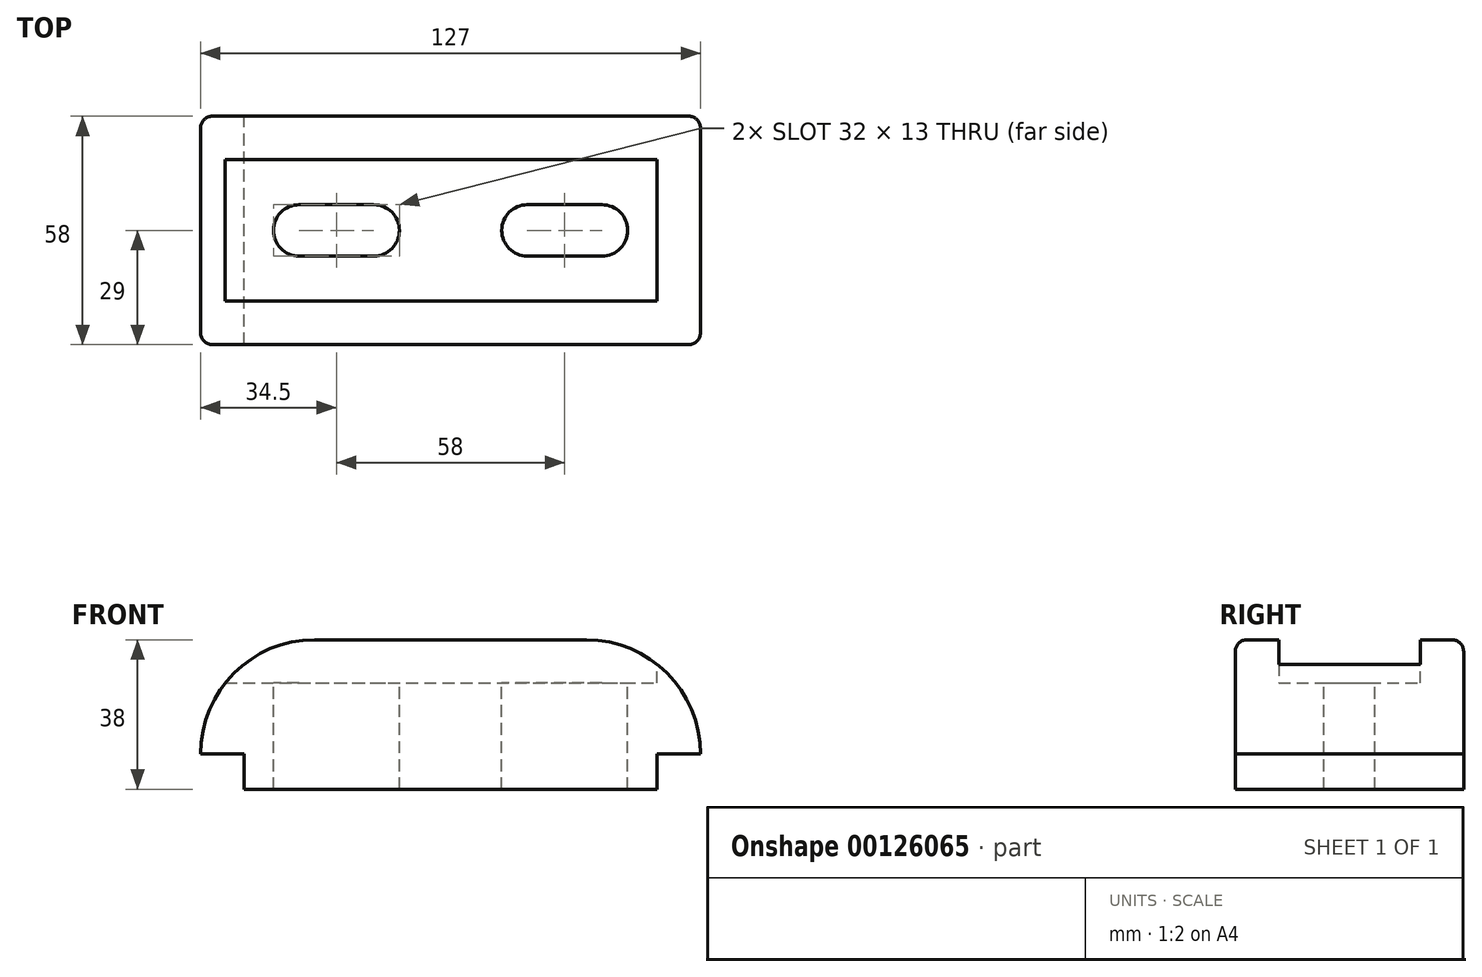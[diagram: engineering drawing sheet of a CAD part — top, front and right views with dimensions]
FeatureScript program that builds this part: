
annotation { "Feature Type Name" : "Feature", "Feature Type Description" : "" }
export const myFeature = defineFeature(function(context is Context, id is Id, definition is map)
    precondition{}
    {
        {
            var Q0;
            Q0=qCreatedBy(makeId("Front.planeOp"),FACE);
            var sketch = newSketch(context, id + "F0", { "sketchPlane" : qUnion([Q0])});
            skLineSegment(sketch, "E0", {"start": v(0, 0) * mm, "end": v(-52.5, 0) * mm});
            skLineSegment(sketch, "E1", {"start": v(-52.5, 0) * mm, "end": v(0, 0) * mm});
            skLineSegment(sketch, "E2.MirrorCS", {"start": v(52.5, 0) * mm, "end": v(0, 0) * mm});
            skLineSegment(sketch, "E3", {"start": v(-52.5, 0) * mm, "end": v(-52.5, 9) * mm});
            skLineSegment(sketch, "E4", {"start": v(-52.5, 9) * mm, "end": v(-63.5, 9) * mm});
            skLineSegment(sketch, "E5", {"start": v(-63.5, 9) * mm, "end": v(-63.5, 9) * mm});
            skLineSegment(sketch, "E6", {"start": v(-34.5, 38) * mm, "end": v(0, 38) * mm});
            skPoint(sketch, "E7.visualSharp", {"position": v(-63.5, 38) * mm});
            skArc(sketch, "E7.filletArc", {"start": v(-34.5, 38) * mm, "mid": v(-55, 29.5) * mm, "end": v(-63.5, 9) * mm});
            skLineSegment(sketch, "E8.MirrorCS", {"start": v(34.5, 38) * mm, "end": v(0, 38) * mm});
            skArc(sketch, "E9.MirrorCS", {"start": v(34.5, 38) * mm, "mid": v(55, 29.5) * mm, "end": v(63.5, 9) * mm});
            skLineSegment(sketch, "E10.MirrorCS", {"start": v(52.5, 9) * mm, "end": v(63.5, 9) * mm});
            skLineSegment(sketch, "E11.MirrorCS", {"start": v(52.5, 0) * mm, "end": v(52.5, 9) * mm});
            skSolve(sketch);
        }
        {
            var Q0;
            Q0 = qSketchRegion(id + "F0", true);
            extrude(context, id + "F1", {"entities" : qUnion([Q0]), "endBound" : BoundingType.SYMMETRIC, "depth" : 58 * mm});
        }
        {
            var Q0;
            Q0=makeQuery(id+"F1.opExtrude","SWEPT_FACE",FACE,{"disambiguationData":[OSD([sQuery(id+"F0.wireOp",EDGE,"E11.MirrorCS")])]});
            var sketch = newSketch(context, id + "F2", { "sketchPlane" : qUnion([Q0])});
            skLineSegment(sketch, "E12", {"start": v(18, 38) * mm, "end": v(-18, 38) * mm});
            skLineSegment(sketch, "E13", {"start": v(-18, 38) * mm, "end": v(-18, 27) * mm});
            skLineSegment(sketch, "E14", {"start": v(-18, 27) * mm, "end": v(18, 27) * mm});
            skLineSegment(sketch, "E15", {"start": v(18, 27) * mm, "end": v(18, 38) * mm});
            skSolve(sketch);
        }
        {
            var Q0;
            Q0 = qSketchRegion(id + "F2", true);
            extrude(context, id + "F3", {"entities" : qUnion([Q0]), "operationType" : NewBodyOperationType.REMOVE, "endBound" : BoundingType.THROUGH_ALL, "oppositeDirection" : true, "depth" : 25 * mm});
        }
        {
            var Q0;
            Q0=makeQuery(id+"F1.opExtrude","CAP_EDGE",EDGE,{"disambiguationData":[OSD([sQuery(id+"F0.wireOp",EDGE,"E6"),sQuery(id+"F0.wireOp",EDGE,"E8.MirrorCS")])],"isStart":true});
            var Q1;
            Q1=makeQuery(id+"F1.opExtrude","CAP_EDGE",EDGE,{"disambiguationData":[OSD([sQuery(id+"F0.wireOp",EDGE,"E6"),sQuery(id+"F0.wireOp",EDGE,"E8.MirrorCS")])],"isStart":false});
            fillet(context, id + "F4", {"entities" : qUnion([Q0, Q1]), "radius" : 3 * mm, "tangentPropagation" : true, "allowEdgeOverflow" : false});
        }
        {
            var Q0;
            Q0=makeQuery(id+"F3.boolean.opBoolean","COPY",FACE,{"derivedFrom":makeQuery(id+"F3.opExtrude","SWEPT_FACE",FACE,{"disambiguationData":[OSD([sQuery(id+"F2.wireOp",EDGE,"E14")])]})});
            var sketch = newSketch(context, id + "F5", { "sketchPlane" : qUnion([Q0])});
            skLineSegment(sketch, "E16.bottom", {"start": v(-38.5, -6.5) * mm, "end": v(-19.5, -6.5) * mm});
            skLineSegment(sketch, "E16.top", {"start": v(-38.5, 6.5) * mm, "end": v(-19.5, 6.5) * mm});
            skLineSegment(sketch, "E16.left", {"start": v(-38.5, -6.5) * mm, "end": v(-38.5, 6.5) * mm});
            skLineSegment(sketch, "E16.right", {"start": v(-19.5, -6.5) * mm, "end": v(-19.5, 6.5) * mm});
            skArc(sketch, "E17", {"start": v(-38.5, 6.5) * mm, "mid": v(-45, 0) * mm, "end": v(-38.5, -6.5) * mm});
            skArc(sketch, "E18", {"start": v(-19.5, 6.5) * mm, "mid": v(-13, 0) * mm, "end": v(-19.5, -6.5) * mm});
            skLineSegment(sketch, "E19.MirrorCS", {"start": v(38.5, 6.5) * mm, "end": v(19.5, 6.5) * mm});
            skLineSegment(sketch, "E20.MirrorCS", {"start": v(38.5, -6.5) * mm, "end": v(19.5, -6.5) * mm});
            skArc(sketch, "E21.MirrorCS", {"start": v(19.5, 6.5) * mm, "mid": v(13, 0) * mm, "end": v(19.5, -6.5) * mm});
            skArc(sketch, "E22.MirrorCS", {"start": v(38.5, 6.5) * mm, "mid": v(45, 0) * mm, "end": v(38.5, -6.5) * mm});
            skLineSegment(sketch, "E23", {"start": v(0, 0) * mm, "end": v(-41.06, 0) * mm, "construction": true});
            skSolve(sketch);
        }
        {
            var Q0;
            Q0=makeQuery(id+"F5.imprint","IMPRINT",FACE,{"disambiguationData":[TD([[makeQuery(id+"F5.imprint","IMPRINT",EDGE,{"derivedFrom":sQuery(id+"F5.wireOp",EDGE,"E16.left")}),1.0]])]});
            var Q1;
            Q1=makeQuery(id+"F5.imprint","IMPRINT",FACE,{"disambiguationData":[TD([[makeQuery(id+"F5.imprint","IMPRINT",EDGE,{"derivedFrom":sQuery(id+"F5.wireOp",EDGE,"E16.bottom")}),1.0]])]});
            var Q2;
            Q2=makeQuery(id+"F5.imprint","IMPRINT",FACE,{"disambiguationData":[TD([[makeQuery(id+"F5.imprint","IMPRINT",EDGE,{"derivedFrom":sQuery(id+"F5.wireOp",EDGE,"E16.right")}),-1.0]])]});
            var Q3;
            Q3=makeQuery(id+"F5.imprint","IMPRINT",FACE,{"disambiguationData":[TD([[makeQuery(id+"F5.imprint","IMPRINT",EDGE,{"derivedFrom":sQuery(id+"F5.wireOp",EDGE,"E19.MirrorCS")}),1.0]])]});
            extrude(context, id + "F6", {"entities" : qUnion([Q0, Q1, Q2, Q3]), "operationType" : NewBodyOperationType.REMOVE, "endBound" : BoundingType.THROUGH_ALL, "oppositeDirection" : true, "depth" : 25 * mm});
        }
    });
